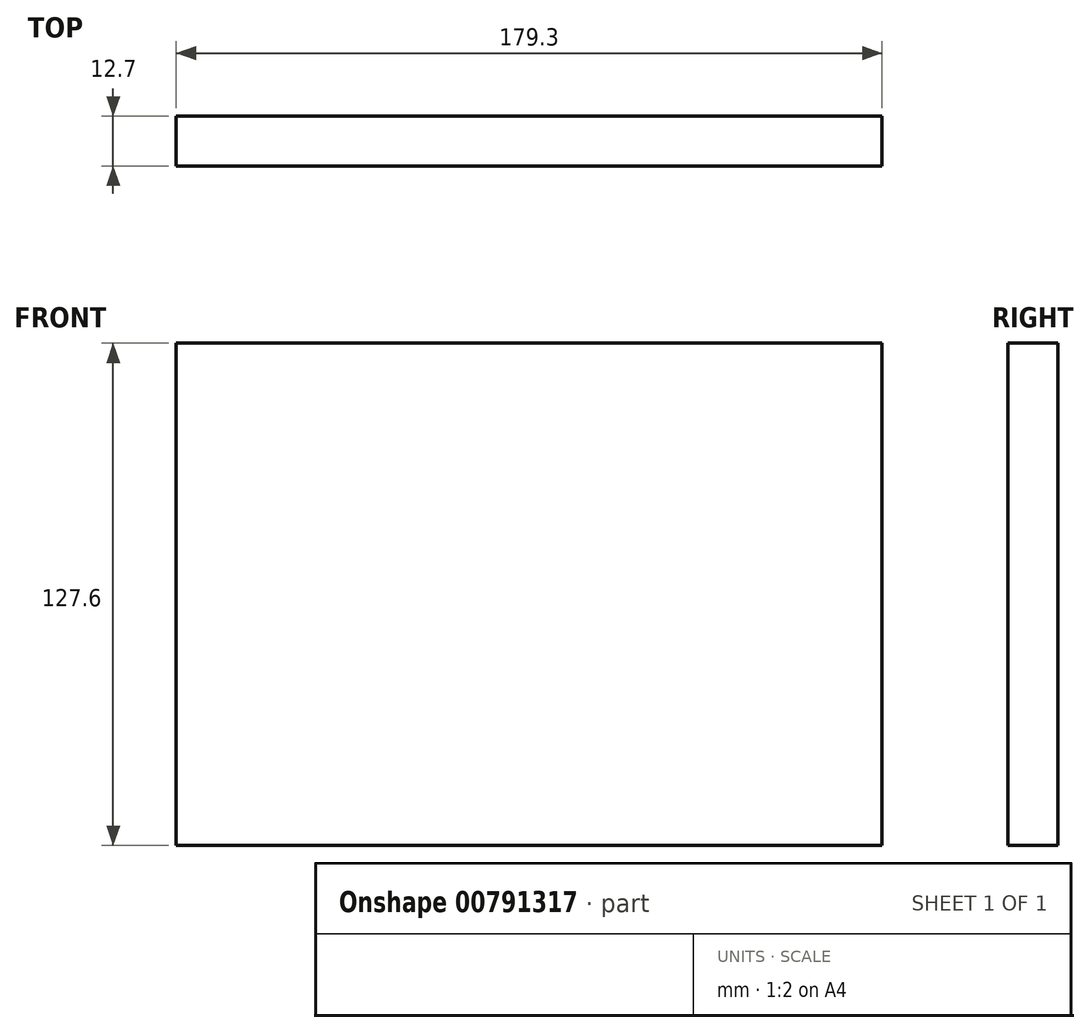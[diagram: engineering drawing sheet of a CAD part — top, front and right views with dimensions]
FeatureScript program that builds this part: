
annotation { "Feature Type Name" : "Feature", "Feature Type Description" : "" }
export const myFeature = defineFeature(function(context is Context, id is Id, definition is map)
    precondition{}
    {
        {
            var Q0;
            Q0=qCreatedBy(makeId("Front.planeOp"),FACE);
            var sketch = newSketch(context, id + "F0", { "sketchPlane" : qUnion([Q0])});
            skLineSegment(sketch, "E0.bottom", {"start": v(-89.65, 63.8) * mm, "end": v(89.65, 63.8) * mm});
            skLineSegment(sketch, "E0.top", {"start": v(-89.65, -63.8) * mm, "end": v(89.65, -63.8) * mm});
            skLineSegment(sketch, "E0.left", {"start": v(-89.65, 63.8) * mm, "end": v(-89.65, -63.8) * mm});
            skLineSegment(sketch, "E0.right", {"start": v(89.65, 63.8) * mm, "end": v(89.65, -63.8) * mm});
            skPoint(sketch, "E0.middle", {"position": v(0, 0) * mm});
            skSolve(sketch);
        }
        {
            var Q0;
            Q0=makeQuery(id+"F0.imprint","IMPRINT",FACE,{"disambiguationData":[TD([[makeQuery(id+"F0.imprint","IMPRINT",EDGE,{"derivedFrom":sQuery(id+"F0.wireOp",EDGE,"E0.bottom")}),-1.0]])]});
            extrude(context, id + "F1", {"entities" : qUnion([Q0]), "depth" : 12.7 * mm, "offsetDistance" : 25.4 * mm});
        }
    });
